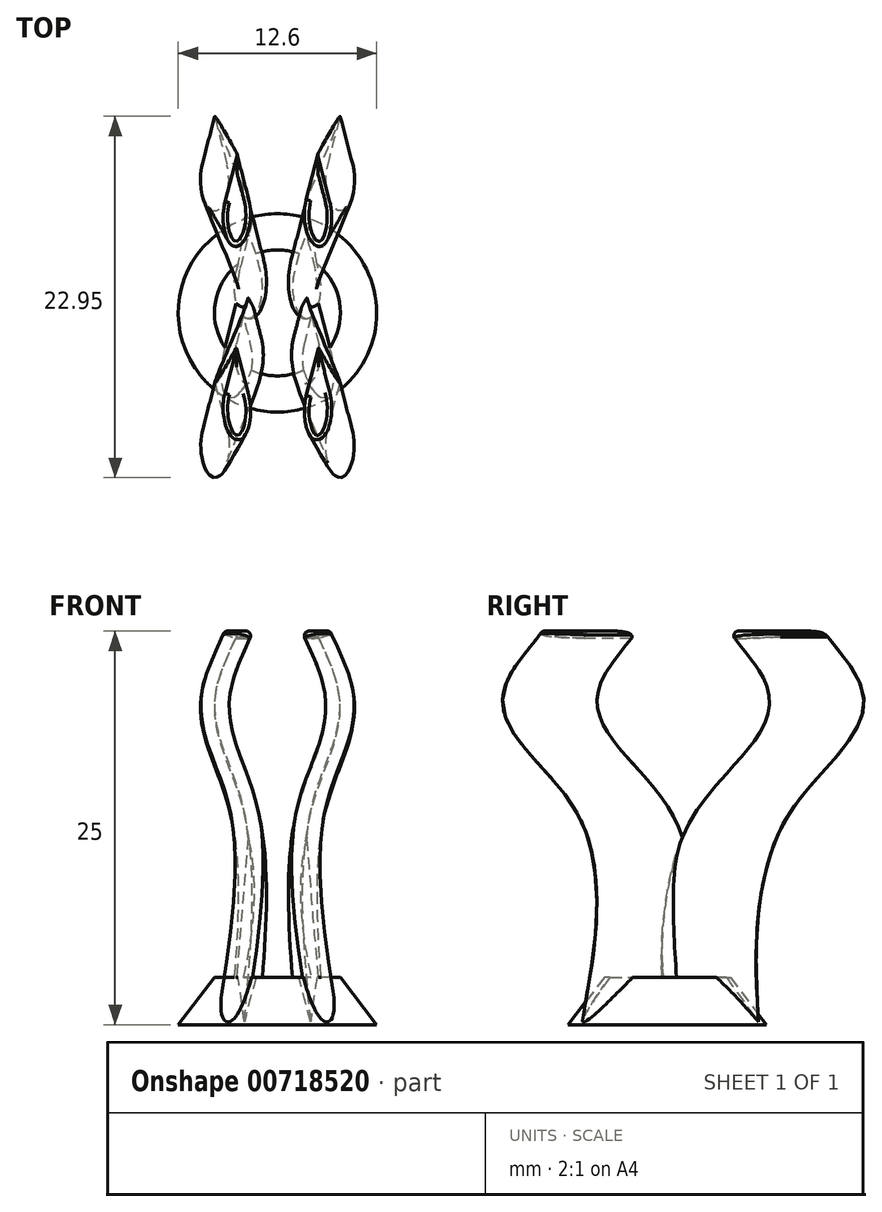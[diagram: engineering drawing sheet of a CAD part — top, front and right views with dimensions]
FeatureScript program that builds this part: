
annotation { "Feature Type Name" : "Feature", "Feature Type Description" : "" }
export const myFeature = defineFeature(function(context is Context, id is Id, definition is map)
    precondition{}
    {
        {
            var Q0;
            Q0=qCreatedBy(makeId("Top.planeOp"),FACE);
            var sketch = newSketch(context, id + "F0", { "sketchPlane" : qUnion([Q0])});
            skCircle(sketch, "E0", {"center": v(0, 0) * mm, "radius": 6.3 * mm});
            skSolve(sketch);
        }
        {
            assignVariable(context, id + "F1", {"variableType" : VariableType.LENGTH, "name" : "BaseHeight", "lengthValue" : 3 * mm});
        }
        {
            var Q0;
            Q0=qCreatedBy(makeId("Top.planeOp"),FACE);
            cPlane(context, id + "F2", {"entities" : qUnion([Q0]), "cplaneType" : CPlaneType.OFFSET, "offset" : getVariable(context, 'BaseHeight'), "width" : 150 * mm, "height" : 150 * mm});
        }
        {
            var Q0;
            Q0=qCreatedBy(id+"F2.planeOp",FACE);
            var sketch = newSketch(context, id + "F3", { "sketchPlane" : qUnion([Q0])});
            skCircle(sketch, "E1", {"center": v(0, 0) * mm, "radius": 4 * mm});
            skSolve(sketch);
        }
        {
            assignVariable(context, id + "F4", {"variableType" : VariableType.LENGTH, "name" : "PostH1", "lengthValue" : 13 * mm});
        }
        {
            assignVariable(context, id + "F5", {"variableType" : VariableType.LENGTH, "name" : "PostH2", "lengthValue" : 18 * mm});
        }
        {
            assignVariable(context, id + "F6", {"variableType" : VariableType.LENGTH, "name" : "PostH3", "lengthValue" : 22 * mm});
        }
        {
            assignVariable(context, id + "F7", {"variableType" : VariableType.LENGTH, "name" : "PostH4", "lengthValue" : 25 * mm});
        }
        {
            var Q0;
            Q0=qCreatedBy(makeId("Top.planeOp"),FACE);
            cPlane(context, id + "F8", {"entities" : qUnion([Q0]), "cplaneType" : CPlaneType.OFFSET, "offset" : getVariable(context, 'PostH1'), "width" : 150 * mm, "height" : 150 * mm});
        }
        {
            var Q0;
            Q0=qCreatedBy(makeId("Top.planeOp"),FACE);
            cPlane(context, id + "F9", {"entities" : qUnion([Q0]), "cplaneType" : CPlaneType.OFFSET, "offset" : getVariable(context, 'PostH2'), "width" : 150 * mm, "height" : 150 * mm});
        }
        {
            var Q0;
            Q0=qCreatedBy(makeId("Top.planeOp"),FACE);
            cPlane(context, id + "F10", {"entities" : qUnion([Q0]), "cplaneType" : CPlaneType.OFFSET, "offset" : getVariable(context, 'PostH3'), "width" : 150 * mm, "height" : 150 * mm});
        }
        {
            var Q0;
            Q0=qCreatedBy(makeId("Top.planeOp"),FACE);
            cPlane(context, id + "F11", {"entities" : qUnion([Q0]), "cplaneType" : CPlaneType.OFFSET, "offset" : getVariable(context, 'PostH4'), "width" : 150 * mm, "height" : 150 * mm});
        }
        {
            var Q0;
            Q0=makeQuery(id+"F0.imprint","IMPRINT",FACE,{"disambiguationData":[TD([[makeQuery(id+"F0.imprint","IMPRINT",EDGE,{"derivedFrom":sQuery(id+"F0.wireOp",EDGE,"E0")}),1.0]])]});
            var Q1;
            Q1=makeQuery(id+"F3.imprint","IMPRINT",FACE,{"disambiguationData":[TD([[makeQuery(id+"F3.imprint","IMPRINT",EDGE,{"derivedFrom":sQuery(id+"F3.wireOp",EDGE,"E1")}),1.0]])]});
            loft(context, id + "F12", {"sheetProfilesArray" : [{ "sheetProfileEntities" : qUnion([Q0]) }, { "sheetProfileEntities" : qUnion([Q1]) }]});
        }
        {
            var Q0;
            Q0=qCreatedBy(makeId("Top.planeOp"),FACE);
            var sketch = newSketch(context, id + "F13", { "sketchPlane" : qUnion([Q0])});
            skEllipse(sketch, "E2", {"center": v(-2.1, 1.8) * mm, "majorRadius": 2 * mm, "minorRadius": 0.9 * mm, "majorAxis": v(0, 1)});
            skLineSegment(sketch, "E3", {"start": v(-2.88, 2.8) * mm, "end": v(-2.1, 5.8) * mm});
            skLineSegment(sketch, "E4", {"start": v(-2.1, 5.8) * mm, "end": v(-1.32, 2.8) * mm});
            skEllipse(sketch, "E5", {"center": v(2.1, 1.8) * mm, "majorRadius": 2 * mm, "minorRadius": 0.9 * mm, "majorAxis": v(0, 1)});
            skLineSegment(sketch, "E6", {"start": v(1.32, 2.8) * mm, "end": v(2.1, 5.8) * mm});
            skLineSegment(sketch, "E7", {"start": v(2.1, 5.8) * mm, "end": v(2.88, 2.8) * mm});
            skEllipse(sketch, "E8", {"center": v(-2.9, -3.4) * mm, "majorRadius": 2 * mm, "minorRadius": 0.9 * mm, "majorAxis": v(0, 1)});
            skLineSegment(sketch, "E9", {"start": v(-3.68, -2.4) * mm, "end": v(-2.9, 0.6) * mm});
            skLineSegment(sketch, "E10", {"start": v(-2.9, 0.6) * mm, "end": v(-2.12, -2.4) * mm});
            skEllipse(sketch, "E11", {"center": v(2.9, -3.4) * mm, "majorRadius": 2 * mm, "minorRadius": 0.9 * mm, "majorAxis": v(0, 1)});
            skLineSegment(sketch, "E12", {"start": v(2.12, -2.4) * mm, "end": v(2.9, 0.6) * mm});
            skLineSegment(sketch, "E13", {"start": v(2.9, 0.6) * mm, "end": v(3.68, -2.4) * mm});
            skSolve(sketch);
        }
        {
            var Q0;
            Q0=qCreatedBy(id+"F8.planeOp",FACE);
            var sketch = newSketch(context, id + "F14", { "sketchPlane" : qUnion([Q0])});
            skEllipse(sketch, "E14", {"center": v(-2, 3.5) * mm, "majorRadius": 2 * mm, "minorRadius": 0.9 * mm, "majorAxis": v(0, 1)});
            skLineSegment(sketch, "E15", {"start": v(-2.78, 4.5) * mm, "end": v(-2, 7.5) * mm});
            skLineSegment(sketch, "E16", {"start": v(-2, 7.5) * mm, "end": v(-1.22, 4.5) * mm});
            skEllipse(sketch, "E17", {"center": v(2, 3.5) * mm, "majorRadius": 2 * mm, "minorRadius": 0.9 * mm, "majorAxis": v(0, 1)});
            skLineSegment(sketch, "E18", {"start": v(1.22, 4.5) * mm, "end": v(2, 7.5) * mm});
            skLineSegment(sketch, "E19", {"start": v(2, 7.5) * mm, "end": v(2.78, 4.5) * mm});
            skEllipse(sketch, "E20", {"center": v(-2, -3.5) * mm, "majorRadius": 2 * mm, "minorRadius": 0.9 * mm, "majorAxis": v(0, 1)});
            skLineSegment(sketch, "E21", {"start": v(-2.78, -2.5) * mm, "end": v(-2, 0.5) * mm});
            skLineSegment(sketch, "E22", {"start": v(-2, 0.5) * mm, "end": v(-1.22, -2.5) * mm});
            skEllipse(sketch, "E23", {"center": v(2, -3.5) * mm, "majorRadius": 2 * mm, "minorRadius": 0.9 * mm, "majorAxis": v(0, 1)});
            skLineSegment(sketch, "E24", {"start": v(1.22, -2.5) * mm, "end": v(2, 0.5) * mm});
            skLineSegment(sketch, "E25", {"start": v(2, 0.5) * mm, "end": v(2.78, -2.5) * mm});
            skSolve(sketch);
        }
        {
            var Q0;
            Q0=qCreatedBy(id+"F10.planeOp",FACE);
            var sketch = newSketch(context, id + "F15", { "sketchPlane" : qUnion([Q0])});
            skEllipse(sketch, "E26", {"center": v(-3.7, 8.1) * mm, "majorRadius": 2 * mm, "minorRadius": 0.9 * mm, "majorAxis": v(0, 1)});
            skLineSegment(sketch, "E27", {"start": v(-4.48, 9.1) * mm, "end": v(-3.7, 12.1) * mm});
            skLineSegment(sketch, "E28", {"start": v(-3.7, 12.1) * mm, "end": v(-2.92, 9.1) * mm});
            skEllipse(sketch, "E29", {"center": v(3.7, 8.1) * mm, "majorRadius": 2 * mm, "minorRadius": 0.9 * mm, "majorAxis": v(0, 1)});
            skLineSegment(sketch, "E30", {"start": v(2.92, 9.1) * mm, "end": v(3.7, 12.1) * mm});
            skLineSegment(sketch, "E31", {"start": v(3.7, 12.1) * mm, "end": v(4.48, 9.1) * mm});
            skEllipse(sketch, "E32", {"center": v(-3.7, -8.1) * mm, "majorRadius": 2 * mm, "minorRadius": 0.9 * mm, "majorAxis": v(0, 1)});
            skLineSegment(sketch, "E33", {"start": v(-4.48, -7.1) * mm, "end": v(-3.7, -4.1) * mm});
            skLineSegment(sketch, "E34", {"start": v(-3.7, -4.1) * mm, "end": v(-2.92, -7.1) * mm});
            skEllipse(sketch, "E35", {"center": v(3.7, -8.1) * mm, "majorRadius": 2 * mm, "minorRadius": 0.9 * mm, "majorAxis": v(0, 1)});
            skLineSegment(sketch, "E36", {"start": v(2.92, -7.1) * mm, "end": v(3.7, -4.1) * mm});
            skLineSegment(sketch, "E37", {"start": v(3.7, -4.1) * mm, "end": v(4.48, -7.1) * mm});
            skSolve(sketch);
        }
        {
            var Q0;
            Q0=qCreatedBy(id+"F11.planeOp",FACE);
            var sketch = newSketch(context, id + "F16", { "sketchPlane" : qUnion([Q0])});
            skEllipse(sketch, "E38", {"center": v(-2.5, 6) * mm, "majorRadius": 2 * mm, "minorRadius": 0.9 * mm, "majorAxis": v(0, 1)});
            skLineSegment(sketch, "E39", {"start": v(-3.28, 7) * mm, "end": v(-2.5, 10) * mm});
            skLineSegment(sketch, "E40", {"start": v(-2.5, 10) * mm, "end": v(-1.72, 7) * mm});
            skEllipse(sketch, "E41", {"center": v(2.5, 6) * mm, "majorRadius": 2 * mm, "minorRadius": 0.9 * mm, "majorAxis": v(0, 1)});
            skLineSegment(sketch, "E42", {"start": v(1.72, 7) * mm, "end": v(2.5, 10) * mm});
            skLineSegment(sketch, "E43", {"start": v(2.5, 10) * mm, "end": v(3.28, 7) * mm});
            skEllipse(sketch, "E44", {"center": v(-2.5, -6) * mm, "majorRadius": 2 * mm, "minorRadius": 0.9 * mm, "majorAxis": v(0, 1)});
            skLineSegment(sketch, "E45", {"start": v(-3.28, -5) * mm, "end": v(-2.5, -2) * mm});
            skLineSegment(sketch, "E46", {"start": v(-2.5, -2) * mm, "end": v(-1.72, -5) * mm});
            skEllipse(sketch, "E47", {"center": v(2.5, -6) * mm, "majorRadius": 2 * mm, "minorRadius": 0.9 * mm, "majorAxis": v(0, 1)});
            skLineSegment(sketch, "E48", {"start": v(1.72, -5) * mm, "end": v(2.5, -2) * mm});
            skLineSegment(sketch, "E49", {"start": v(2.5, -2) * mm, "end": v(3.28, -5) * mm});
            skSolve(sketch);
        }
        {
            assignVariable(context, id + "F17", {"variableType" : VariableType.NUMBER, "name" : "Loft1", "numberValue" : 0.3});
        }
        {
            var Q0;
            {var subQ0=sQuery(id+"F13.wireOp",EDGE,"E5");var subQ1=makeQuery(id+"F13.imprint","INTERSECT",VERTEX,{"derivedFrom":[subQ0,sQuery(id+"F13.wireOp",EDGE,"E6")]});Q0=makeQuery(id+"F13.imprint","IMPRINT",FACE,{"disambiguationData":[TD([[makeQuery(id+"F13.imprint","IMPRINT",EDGE,{"disambiguationData":[TD([[subQ1,-1.0]])],"derivedFrom":subQ0}),1.0]])]});}
            var Q1;
            {var subQ0=sQuery(id+"F13.wireOp",EDGE,"E6");Q1=makeQuery(id+"F13.imprint","IMPRINT",FACE,{"disambiguationData":[TD([[makeQuery(id+"F13.imprint","IMPRINT",EDGE,{"derivedFrom":subQ0}),-1.0]])]});}
            var Q2;
            {var subQ0=sQuery(id+"F14.wireOp",EDGE,"E17");var subQ1=makeQuery(id+"F14.imprint","INTERSECT",VERTEX,{"derivedFrom":[subQ0,sQuery(id+"F14.wireOp",EDGE,"E18")]});Q2=makeQuery(id+"F14.imprint","IMPRINT",FACE,{"disambiguationData":[TD([[makeQuery(id+"F14.imprint","IMPRINT",EDGE,{"disambiguationData":[TD([[subQ1,-1.0]])],"derivedFrom":subQ0}),1.0]])]});}
            var Q3;
            {var subQ0=sQuery(id+"F14.wireOp",EDGE,"E18");Q3=makeQuery(id+"F14.imprint","IMPRINT",FACE,{"disambiguationData":[TD([[makeQuery(id+"F14.imprint","IMPRINT",EDGE,{"derivedFrom":subQ0}),-1.0]])]});}
            var Q4;
            {var subQ0=sQuery(id+"F15.wireOp",EDGE,"E29");var subQ1=makeQuery(id+"F15.imprint","INTERSECT",VERTEX,{"derivedFrom":[subQ0,sQuery(id+"F15.wireOp",EDGE,"E30")]});Q4=makeQuery(id+"F15.imprint","IMPRINT",FACE,{"disambiguationData":[TD([[makeQuery(id+"F15.imprint","IMPRINT",EDGE,{"disambiguationData":[TD([[subQ1,-1.0]])],"derivedFrom":subQ0}),1.0]])]});}
            var Q5;
            {var subQ0=sQuery(id+"F15.wireOp",EDGE,"E30");Q5=makeQuery(id+"F15.imprint","IMPRINT",FACE,{"disambiguationData":[TD([[makeQuery(id+"F15.imprint","IMPRINT",EDGE,{"derivedFrom":subQ0}),-1.0]])]});}
            var Q6;
            {var subQ0=sQuery(id+"F16.wireOp",EDGE,"E41");var subQ1=makeQuery(id+"F16.imprint","INTERSECT",VERTEX,{"derivedFrom":[subQ0,sQuery(id+"F16.wireOp",EDGE,"E42")]});Q6=makeQuery(id+"F16.imprint","IMPRINT",FACE,{"disambiguationData":[TD([[makeQuery(id+"F16.imprint","IMPRINT",EDGE,{"disambiguationData":[TD([[subQ1,-1.0]])],"derivedFrom":subQ0}),1.0]])]});}
            var Q7;
            {var subQ0=sQuery(id+"F16.wireOp",EDGE,"E42");Q7=makeQuery(id+"F16.imprint","IMPRINT",FACE,{"disambiguationData":[TD([[makeQuery(id+"F16.imprint","IMPRINT",EDGE,{"derivedFrom":subQ0}),-1.0]])]});}
            loft(context, id + "F18", {"operationType" : NewBodyOperationType.ADD, "sheetProfilesArray" : [{ "sheetProfileEntities" : qUnion([Q0, Q1]) }, { "sheetProfileEntities" : qUnion([Q2, Q3]) }, { "sheetProfileEntities" : qUnion([Q4, Q5]) }, { "sheetProfileEntities" : qUnion([Q6, Q7]) }], "startCondition" : LoftEndDerivativeType.NORMAL_TO_PROFILE, "startMagnitude" : getVariable(context, 'Loft1'), "endCondition" : LoftEndDerivativeType.NORMAL_TO_PROFILE, "endMagnitude" : getVariable(context, 'Loft1')});
        }
        {
            var Q0;
            {var subQ0=sQuery(id+"F13.wireOp",EDGE,"E3");Q0=makeQuery(id+"F13.imprint","IMPRINT",FACE,{"disambiguationData":[TD([[makeQuery(id+"F13.imprint","IMPRINT",EDGE,{"derivedFrom":subQ0}),-1.0]])]});}
            var Q1;
            {var subQ0=sQuery(id+"F13.wireOp",EDGE,"E2");var subQ1=makeQuery(id+"F13.imprint","INTERSECT",VERTEX,{"derivedFrom":[subQ0,sQuery(id+"F13.wireOp",EDGE,"E3")]});Q1=makeQuery(id+"F13.imprint","IMPRINT",FACE,{"disambiguationData":[TD([[makeQuery(id+"F13.imprint","IMPRINT",EDGE,{"disambiguationData":[TD([[subQ1,-1.0]])],"derivedFrom":subQ0}),1.0]])]});}
            var Q2;
            {var subQ0=sQuery(id+"F14.wireOp",EDGE,"E15");Q2=makeQuery(id+"F14.imprint","IMPRINT",FACE,{"disambiguationData":[TD([[makeQuery(id+"F14.imprint","IMPRINT",EDGE,{"derivedFrom":subQ0}),-1.0]])]});}
            var Q3;
            {var subQ0=sQuery(id+"F14.wireOp",EDGE,"E14");var subQ1=makeQuery(id+"F14.imprint","INTERSECT",VERTEX,{"derivedFrom":[subQ0,sQuery(id+"F14.wireOp",EDGE,"E15")]});Q3=makeQuery(id+"F14.imprint","IMPRINT",FACE,{"disambiguationData":[TD([[makeQuery(id+"F14.imprint","IMPRINT",EDGE,{"disambiguationData":[TD([[subQ1,-1.0]])],"derivedFrom":subQ0}),1.0]])]});}
            var Q4;
            {var subQ0=sQuery(id+"F15.wireOp",EDGE,"E26");var subQ1=makeQuery(id+"F15.imprint","INTERSECT",VERTEX,{"derivedFrom":[subQ0,sQuery(id+"F15.wireOp",EDGE,"E27")]});Q4=makeQuery(id+"F15.imprint","IMPRINT",FACE,{"disambiguationData":[TD([[makeQuery(id+"F15.imprint","IMPRINT",EDGE,{"disambiguationData":[TD([[subQ1,-1.0]])],"derivedFrom":subQ0}),1.0]])]});}
            var Q5;
            {var subQ0=sQuery(id+"F15.wireOp",EDGE,"E27");Q5=makeQuery(id+"F15.imprint","IMPRINT",FACE,{"disambiguationData":[TD([[makeQuery(id+"F15.imprint","IMPRINT",EDGE,{"derivedFrom":subQ0}),-1.0]])]});}
            var Q6;
            {var subQ0=sQuery(id+"F16.wireOp",EDGE,"E38");var subQ1=makeQuery(id+"F16.imprint","INTERSECT",VERTEX,{"derivedFrom":[subQ0,sQuery(id+"F16.wireOp",EDGE,"E39")]});Q6=makeQuery(id+"F16.imprint","IMPRINT",FACE,{"disambiguationData":[TD([[makeQuery(id+"F16.imprint","IMPRINT",EDGE,{"disambiguationData":[TD([[subQ1,-1.0]])],"derivedFrom":subQ0}),1.0]])]});}
            var Q7;
            {var subQ0=sQuery(id+"F16.wireOp",EDGE,"E39");Q7=makeQuery(id+"F16.imprint","IMPRINT",FACE,{"disambiguationData":[TD([[makeQuery(id+"F16.imprint","IMPRINT",EDGE,{"derivedFrom":subQ0}),-1.0]])]});}
            loft(context, id + "F19", {"operationType" : NewBodyOperationType.ADD, "sheetProfilesArray" : [{ "sheetProfileEntities" : qUnion([Q0, Q1]) }, { "sheetProfileEntities" : qUnion([Q2, Q3]) }, { "sheetProfileEntities" : qUnion([Q4, Q5]) }, { "sheetProfileEntities" : qUnion([Q6, Q7]) }], "startCondition" : LoftEndDerivativeType.NORMAL_TO_PROFILE, "startMagnitude" : getVariable(context, 'Loft1'), "endCondition" : LoftEndDerivativeType.NORMAL_TO_PROFILE, "endMagnitude" : getVariable(context, 'Loft1')});
        }
        {
            var Q0;
            {var subQ0=sQuery(id+"F13.wireOp",EDGE,"E9");Q0=makeQuery(id+"F13.imprint","IMPRINT",FACE,{"disambiguationData":[TD([[makeQuery(id+"F13.imprint","IMPRINT",EDGE,{"derivedFrom":subQ0}),-1.0]])]});}
            var Q1;
            {var subQ0=sQuery(id+"F13.wireOp",EDGE,"E8");var subQ1=makeQuery(id+"F13.imprint","INTERSECT",VERTEX,{"derivedFrom":[subQ0,sQuery(id+"F13.wireOp",EDGE,"E9")]});Q1=makeQuery(id+"F13.imprint","IMPRINT",FACE,{"disambiguationData":[TD([[makeQuery(id+"F13.imprint","IMPRINT",EDGE,{"disambiguationData":[TD([[subQ1,-1.0]])],"derivedFrom":subQ0}),1.0]])]});}
            var Q2;
            {var subQ0=sQuery(id+"F14.wireOp",EDGE,"E21");Q2=makeQuery(id+"F14.imprint","IMPRINT",FACE,{"disambiguationData":[TD([[makeQuery(id+"F14.imprint","IMPRINT",EDGE,{"derivedFrom":subQ0}),-1.0]])]});}
            var Q3;
            {var subQ0=sQuery(id+"F14.wireOp",EDGE,"E20");var subQ1=makeQuery(id+"F14.imprint","INTERSECT",VERTEX,{"derivedFrom":[subQ0,sQuery(id+"F14.wireOp",EDGE,"E21")]});Q3=makeQuery(id+"F14.imprint","IMPRINT",FACE,{"disambiguationData":[TD([[makeQuery(id+"F14.imprint","IMPRINT",EDGE,{"disambiguationData":[TD([[subQ1,-1.0]])],"derivedFrom":subQ0}),1.0]])]});}
            var Q4;
            {var subQ0=sQuery(id+"F15.wireOp",EDGE,"E32");var subQ1=makeQuery(id+"F15.imprint","INTERSECT",VERTEX,{"derivedFrom":[subQ0,sQuery(id+"F15.wireOp",EDGE,"E33")]});Q4=makeQuery(id+"F15.imprint","IMPRINT",FACE,{"disambiguationData":[TD([[makeQuery(id+"F15.imprint","IMPRINT",EDGE,{"disambiguationData":[TD([[subQ1,-1.0]])],"derivedFrom":subQ0}),1.0]])]});}
            var Q5;
            {var subQ0=sQuery(id+"F15.wireOp",EDGE,"E33");Q5=makeQuery(id+"F15.imprint","IMPRINT",FACE,{"disambiguationData":[TD([[makeQuery(id+"F15.imprint","IMPRINT",EDGE,{"derivedFrom":subQ0}),-1.0]])]});}
            var Q6;
            {var subQ0=sQuery(id+"F16.wireOp",EDGE,"E44");var subQ1=makeQuery(id+"F16.imprint","INTERSECT",VERTEX,{"derivedFrom":[subQ0,sQuery(id+"F16.wireOp",EDGE,"E45")]});Q6=makeQuery(id+"F16.imprint","IMPRINT",FACE,{"disambiguationData":[TD([[makeQuery(id+"F16.imprint","IMPRINT",EDGE,{"disambiguationData":[TD([[subQ1,-1.0]])],"derivedFrom":subQ0}),1.0]])]});}
            var Q7;
            {var subQ0=sQuery(id+"F16.wireOp",EDGE,"E45");Q7=makeQuery(id+"F16.imprint","IMPRINT",FACE,{"disambiguationData":[TD([[makeQuery(id+"F16.imprint","IMPRINT",EDGE,{"derivedFrom":subQ0}),-1.0]])]});}
            loft(context, id + "F20", {"operationType" : NewBodyOperationType.ADD, "sheetProfilesArray" : [{ "sheetProfileEntities" : qUnion([Q0, Q1]) }, { "sheetProfileEntities" : qUnion([Q2, Q3]) }, { "sheetProfileEntities" : qUnion([Q4, Q5]) }, { "sheetProfileEntities" : qUnion([Q6, Q7]) }], "startCondition" : LoftEndDerivativeType.NORMAL_TO_PROFILE, "startMagnitude" : getVariable(context, 'Loft1'), "endCondition" : LoftEndDerivativeType.NORMAL_TO_PROFILE, "endMagnitude" : getVariable(context, 'Loft1')});
        }
        {
            var Q0;
            {var subQ0=sQuery(id+"F13.wireOp",EDGE,"E11");var subQ1=makeQuery(id+"F13.imprint","INTERSECT",VERTEX,{"derivedFrom":[subQ0,sQuery(id+"F13.wireOp",EDGE,"E12")]});Q0=makeQuery(id+"F13.imprint","IMPRINT",FACE,{"disambiguationData":[TD([[makeQuery(id+"F13.imprint","IMPRINT",EDGE,{"disambiguationData":[TD([[subQ1,-1.0]])],"derivedFrom":subQ0}),1.0]])]});}
            var Q1;
            {var subQ0=sQuery(id+"F13.wireOp",EDGE,"E12");Q1=makeQuery(id+"F13.imprint","IMPRINT",FACE,{"disambiguationData":[TD([[makeQuery(id+"F13.imprint","IMPRINT",EDGE,{"derivedFrom":subQ0}),-1.0]])]});}
            var Q2;
            {var subQ0=sQuery(id+"F14.wireOp",EDGE,"E23");var subQ1=makeQuery(id+"F14.imprint","INTERSECT",VERTEX,{"derivedFrom":[subQ0,sQuery(id+"F14.wireOp",EDGE,"E24")]});Q2=makeQuery(id+"F14.imprint","IMPRINT",FACE,{"disambiguationData":[TD([[makeQuery(id+"F14.imprint","IMPRINT",EDGE,{"disambiguationData":[TD([[subQ1,-1.0]])],"derivedFrom":subQ0}),1.0]])]});}
            var Q3;
            {var subQ0=sQuery(id+"F14.wireOp",EDGE,"E24");Q3=makeQuery(id+"F14.imprint","IMPRINT",FACE,{"disambiguationData":[TD([[makeQuery(id+"F14.imprint","IMPRINT",EDGE,{"derivedFrom":subQ0}),-1.0]])]});}
            var Q4;
            {var subQ0=sQuery(id+"F15.wireOp",EDGE,"E35");var subQ1=makeQuery(id+"F15.imprint","INTERSECT",VERTEX,{"derivedFrom":[subQ0,sQuery(id+"F15.wireOp",EDGE,"E36")]});Q4=makeQuery(id+"F15.imprint","IMPRINT",FACE,{"disambiguationData":[TD([[makeQuery(id+"F15.imprint","IMPRINT",EDGE,{"disambiguationData":[TD([[subQ1,-1.0]])],"derivedFrom":subQ0}),1.0]])]});}
            var Q5;
            {var subQ0=sQuery(id+"F15.wireOp",EDGE,"E36");Q5=makeQuery(id+"F15.imprint","IMPRINT",FACE,{"disambiguationData":[TD([[makeQuery(id+"F15.imprint","IMPRINT",EDGE,{"derivedFrom":subQ0}),-1.0]])]});}
            var Q6;
            {var subQ0=sQuery(id+"F16.wireOp",EDGE,"E47");var subQ1=makeQuery(id+"F16.imprint","INTERSECT",VERTEX,{"derivedFrom":[subQ0,sQuery(id+"F16.wireOp",EDGE,"E48")]});Q6=makeQuery(id+"F16.imprint","IMPRINT",FACE,{"disambiguationData":[TD([[makeQuery(id+"F16.imprint","IMPRINT",EDGE,{"disambiguationData":[TD([[subQ1,-1.0]])],"derivedFrom":subQ0}),1.0]])]});}
            var Q7;
            {var subQ0=sQuery(id+"F16.wireOp",EDGE,"E48");Q7=makeQuery(id+"F16.imprint","IMPRINT",FACE,{"disambiguationData":[TD([[makeQuery(id+"F16.imprint","IMPRINT",EDGE,{"derivedFrom":subQ0}),-1.0]])]});}
            loft(context, id + "F21", {"operationType" : NewBodyOperationType.ADD, "sheetProfilesArray" : [{ "sheetProfileEntities" : qUnion([Q0, Q1]) }, { "sheetProfileEntities" : qUnion([Q2, Q3]) }, { "sheetProfileEntities" : qUnion([Q4, Q5]) }, { "sheetProfileEntities" : qUnion([Q6, Q7]) }], "startCondition" : LoftEndDerivativeType.NORMAL_TO_PROFILE, "startMagnitude" : getVariable(context, 'Loft1'), "endCondition" : LoftEndDerivativeType.NORMAL_TO_PROFILE, "endMagnitude" : getVariable(context, 'Loft1')});
        }
        {
            var Q0;
            {var subQ0=sQuery(id+"F16.wireOp",EDGE,"E45");var subQ1=sQuery(id+"F16.wireOp",EDGE,"E44");var subQ2=makeQuery(id+"F16.imprint","INTERSECT",VERTEX,{"derivedFrom":[subQ1,subQ0]});Q0=makeQuery(id+"F20.opLoft","CAP_FACE",FACE,{"disambiguationData":[OSD([makeQuery(id+"F16.imprint","IMPRINT",FACE,{"disambiguationData":[TD([[makeQuery(id+"F16.imprint","IMPRINT",EDGE,{"disambiguationData":[TD([[subQ2,-1.0]])],"derivedFrom":subQ1}),1.0]])]}),makeQuery(id+"F16.imprint","IMPRINT",FACE,{"disambiguationData":[TD([[makeQuery(id+"F16.imprint","IMPRINT",EDGE,{"derivedFrom":subQ0}),-1.0]])]})])],"isStart":true});}
            var Q1;
            {var subQ0=sQuery(id+"F16.wireOp",EDGE,"E39");var subQ1=sQuery(id+"F16.wireOp",EDGE,"E38");var subQ2=makeQuery(id+"F16.imprint","INTERSECT",VERTEX,{"derivedFrom":[subQ1,subQ0]});Q1=makeQuery(id+"F19.opLoft","CAP_FACE",FACE,{"disambiguationData":[OSD([makeQuery(id+"F16.imprint","IMPRINT",FACE,{"disambiguationData":[TD([[makeQuery(id+"F16.imprint","IMPRINT",EDGE,{"disambiguationData":[TD([[subQ2,-1.0]])],"derivedFrom":subQ1}),1.0]])]}),makeQuery(id+"F16.imprint","IMPRINT",FACE,{"disambiguationData":[TD([[makeQuery(id+"F16.imprint","IMPRINT",EDGE,{"derivedFrom":subQ0}),-1.0]])]})])],"isStart":true});}
            var Q2;
            {var subQ0=sQuery(id+"F16.wireOp",EDGE,"E48");var subQ1=sQuery(id+"F16.wireOp",EDGE,"E47");var subQ2=makeQuery(id+"F16.imprint","INTERSECT",VERTEX,{"derivedFrom":[subQ1,subQ0]});Q2=makeQuery(id+"F21.opLoft","CAP_FACE",FACE,{"disambiguationData":[OSD([makeQuery(id+"F16.imprint","IMPRINT",FACE,{"disambiguationData":[TD([[makeQuery(id+"F16.imprint","IMPRINT",EDGE,{"disambiguationData":[TD([[subQ2,-1.0]])],"derivedFrom":subQ1}),1.0]])]}),makeQuery(id+"F16.imprint","IMPRINT",FACE,{"disambiguationData":[TD([[makeQuery(id+"F16.imprint","IMPRINT",EDGE,{"derivedFrom":subQ0}),-1.0]])]})])],"isStart":true});}
            var Q3;
            {var subQ0=sQuery(id+"F16.wireOp",EDGE,"E42");var subQ1=sQuery(id+"F16.wireOp",EDGE,"E41");var subQ2=makeQuery(id+"F16.imprint","INTERSECT",VERTEX,{"derivedFrom":[subQ1,subQ0]});Q3=makeQuery(id+"F18.opLoft","CAP_FACE",FACE,{"disambiguationData":[OSD([makeQuery(id+"F16.imprint","IMPRINT",FACE,{"disambiguationData":[TD([[makeQuery(id+"F16.imprint","IMPRINT",EDGE,{"disambiguationData":[TD([[subQ2,-1.0]])],"derivedFrom":subQ1}),1.0]])]}),makeQuery(id+"F16.imprint","IMPRINT",FACE,{"disambiguationData":[TD([[makeQuery(id+"F16.imprint","IMPRINT",EDGE,{"derivedFrom":subQ0}),-1.0]])]})])],"isStart":true});}
            fillet(context, id + "F22", {"entities" : qUnion([Q0, Q1, Q2, Q3]), "tangentPropagation" : true, "radius" : .3 * mm, "defaultsChanged" : true, "isVariable" : true, "vertexSettings" : [], "smoothTransition" : true});
        }
    });
